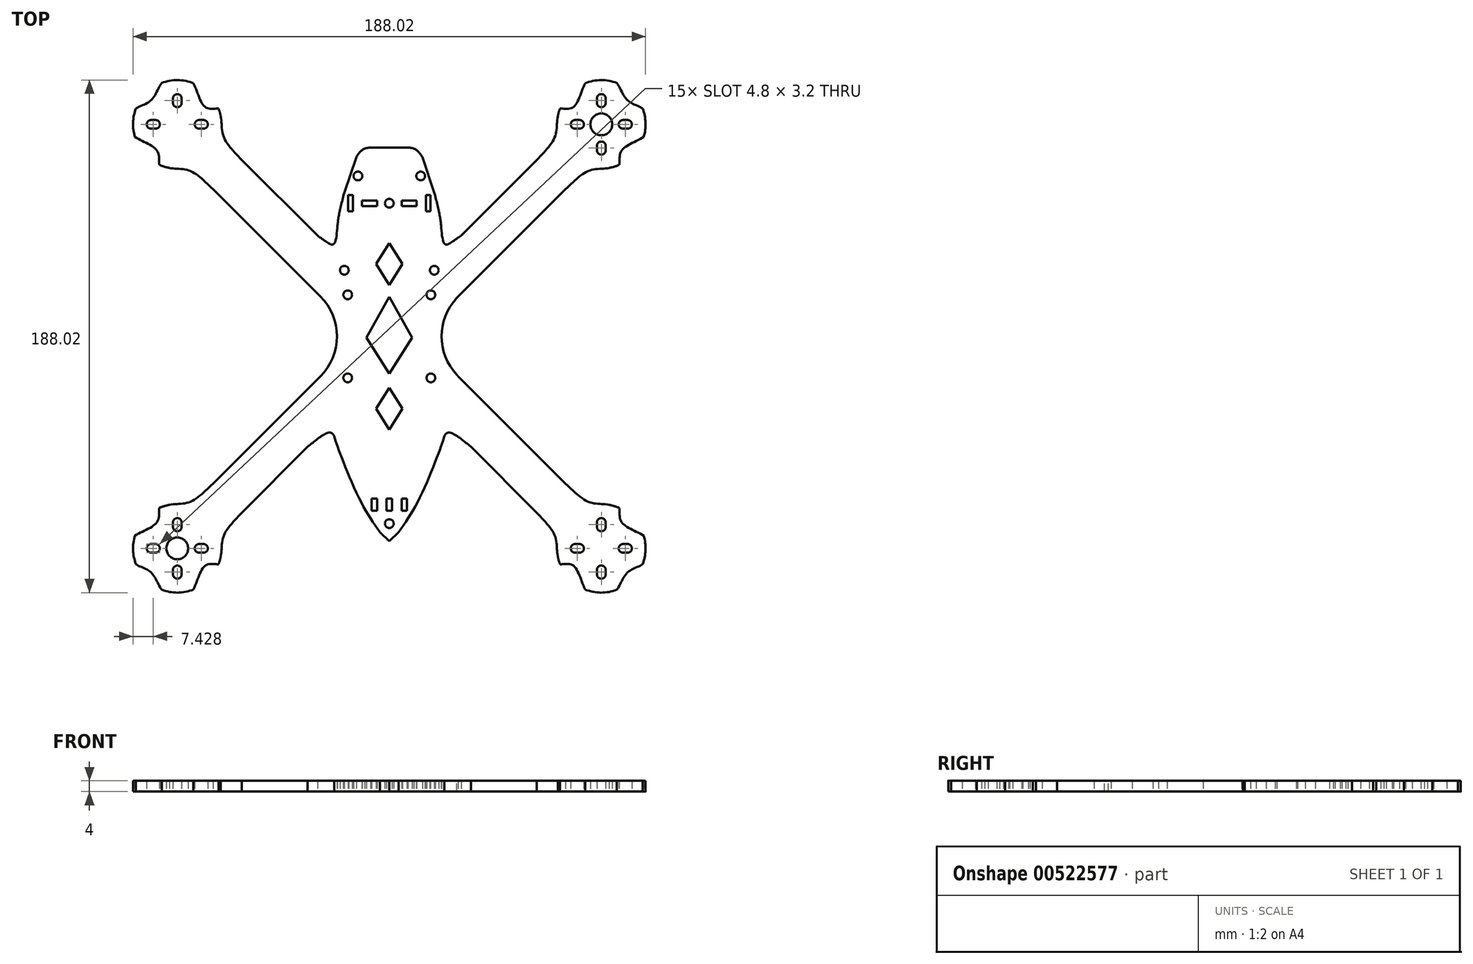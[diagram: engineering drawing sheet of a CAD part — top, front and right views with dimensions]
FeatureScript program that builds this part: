
annotation { "Feature Type Name" : "Feature", "Feature Type Description" : "" }
export const myFeature = defineFeature(function(context is Context, id is Id, definition is map)
    precondition{}
    {
        {
            var Q0;
            Q0=qCreatedBy(makeId("Top.planeOp"),FACE);
            var sketch = newSketch(context, id + "F0", { "sketchPlane" : qUnion([Q0])});
            skArc(sketch, "E0", {"start": v(79.38, 87.28) * mm, "mid": v(77.78, 88.88) * mm, "end": v(76.18, 87.28) * mm});
            skArc(sketch, "E1", {"start": v(69.78, 76.18) * mm, "mid": v(71.38, 77.78) * mm, "end": v(69.78, 79.38) * mm});
            skArc(sketch, "E2", {"start": v(76.18, 68.28) * mm, "mid": v(77.78, 66.68) * mm, "end": v(79.38, 68.28) * mm});
            skFitSpline(sketch, "E3", {"points": [v(54.07, 64.68) * mm, v(60.8, 73.32) * mm, v(61.81, 80.69) * mm], "startDerivative": vector(14.32, 15.77) * mm, "endDerivative": vector(3.24, 15.8) * mm});
            skFitSpline(sketch, "E4.MirrorCS", {"points": [v(64.68, 54.07) * mm, v(73.32, 60.8) * mm, v(80.69, 61.81) * mm], "startDerivative": vector(15.77, 14.32) * mm, "endDerivative": vector(15.8, 3.24) * mm});
            skArc(sketch, "E5.MirrorC", {"start": v(71.84, 92.89) * mm, "mid": v(77.65, 94.01) * mm, "end": v(83.48, 92.98) * mm});
            skArc(sketch, "E6.trimOffspring", {"start": v(61.81, 80.69) * mm, "mid": v(62.15, 82.16) * mm, "end": v(62.63, 83.6) * mm});
            skFitSpline(sketch, "E7", {"points": [v(62.63, 83.6) * mm, v(67.35, 84.01) * mm, v(71.84, 92.89) * mm], "startDerivative": vector(9.44, 0.18) * mm, "endDerivative": vector(7.72, 15.8) * mm});
            skFitSpline(sketch, "E8", {"points": [v(84.37, 62.95) * mm, v(85.15, 68.03) * mm, v(93.33, 73.14) * mm], "startDerivative": vector(1.43, 9.82) * mm, "endDerivative": vector(14.32, 9.05) * mm});
            skFitSpline(sketch, "E9", {"points": [v(92.94, 83.58) * mm, v(87.34, 86.65) * mm, v(83.48, 92.98) * mm], "startDerivative": vector(-9.53, 6.72) * mm, "endDerivative": vector(-7.98, 10.57) * mm});
            skArc(sketch, "E10.trimOffspring", {"start": v(92.94, 83.58) * mm, "mid": v(94, 78.4) * mm, "end": v(93.33, 73.14) * mm});
            skArc(sketch, "E11.trimOffspring", {"start": v(84.37, 62.95) * mm, "mid": v(82.56, 62.27) * mm, "end": v(80.69, 61.81) * mm});
            skCircle(sketch, "E12", {"center": v(77.78, 77.78) * mm, "radius": 4 * mm});
            skCircle(sketch, "E13.MirrorC", {"center": v(-77.78, 77.78) * mm, "radius": 4 * mm});
            skLineSegment(sketch, "E14.MirrorCS", {"start": v(-25.3, 14.68) * mm, "end": v(-64.68, 54.07) * mm});
            skCircle(sketch, "E15.MirrorC", {"center": v(77.78, -77.78) * mm, "radius": 4 * mm});
            skCircle(sketch, "E16.MirrorC", {"center": v(-77.78, -77.78) * mm, "radius": 4 * mm});
            skLineSegment(sketch, "E17.MirrorCS", {"start": v(-25.3, -14.68) * mm, "end": v(-64.68, -54.07) * mm});
            skLineSegment(sketch, "E18.MirrorCS", {"start": v(25.3, -14.68) * mm, "end": v(64.68, -54.07) * mm});
            skLineSegment(sketch, "E19.MirrorCS", {"start": v(27.36, -37.96) * mm, "end": v(54.07, -64.68) * mm});
            skLineSegment(sketch, "E20.MirrorCS", {"start": v(-27.36, -37.96) * mm, "end": v(-54.07, -64.68) * mm});
            skLineSegment(sketch, "E21.trimOffspring", {"start": v(-26.35, 36.96) * mm, "end": v(-54.07, 64.68) * mm});
            skLineSegment(sketch, "E22.trimOffspring", {"start": v(26.35, 36.96) * mm, "end": v(54.07, 64.68) * mm});
            skFitSpline(sketch, "E23", {"points": [v(29.93, -40.53) * mm, v(24.71, -36.48) * mm, v(21.1, -35.5) * mm, v(19, -47.4) * mm], "startDerivative": vector(-16.04, 13.48) * mm, "endDerivative": vector(-1.52, -37.22) * mm});
            skFitSpline(sketch, "E24.MirrorCS", {"points": [v(-29.93, -40.53) * mm, v(-24.71, -36.48) * mm, v(-21.1, -35.5) * mm, v(-19, -47.4) * mm], "startDerivative": vector(16.04, 13.48) * mm, "endDerivative": vector(1.52, -37.22) * mm});
            skFitSpline(sketch, "E25", {"points": [v(-12.14, 65.75) * mm, v(-10.16, 68.18) * mm, v(-6.56, 70) * mm], "startDerivative": vector(3.6, 5.61) * mm, "endDerivative": vector(7.46, 2.94) * mm});
            skFitSpline(sketch, "E26", {"points": [v(-19, 40.7) * mm, v(-18.4, 44.88) * mm, v(-16.56, 52.62) * mm], "startDerivative": vector(1.06, 9.2) * mm, "endDerivative": vector(3.7, 14.37) * mm});
            skLineSegment(sketch, "E27", {"start": v(-16.56, 52.62) * mm, "end": v(-12.14, 65.75) * mm});
            skFitSpline(sketch, "E28.MirrorCS", {"points": [v(12.14, 65.75) * mm, v(10.16, 68.18) * mm, v(6.56, 70) * mm], "startDerivative": vector(-3.6, 5.61) * mm, "endDerivative": vector(-7.46, 2.94) * mm});
            skFitSpline(sketch, "E29.MirrorCS", {"points": [v(19, 40.7) * mm, v(18.4, 44.88) * mm, v(16.56, 52.62) * mm], "startDerivative": vector(-1.06, 9.2) * mm, "endDerivative": vector(-3.7, 14.37) * mm});
            skLineSegment(sketch, "E30.MirrorCS", {"start": v(16.56, 52.62) * mm, "end": v(12.14, 65.75) * mm});
            skFitSpline(sketch, "E31", {"points": [v(-9.06, 68.9) * mm, v(-6.8, 69.3) * mm, v(-4.56, 69.08) * mm], "startDerivative": vector(4.47, 1.15) * mm, "endDerivative": vector(4.51, -0.76) * mm});
            skFitSpline(sketch, "E32.MirrorCS", {"points": [v(9.06, 68.9) * mm, v(6.8, 69.3) * mm, v(4.56, 69.08) * mm], "startDerivative": vector(-4.47, 1.15) * mm, "endDerivative": vector(-4.51, -0.76) * mm});
            skFitSpline(sketch, "E33.MirrorCS", {"points": [v(25.3, 14.68) * mm, v(21.09, 9.2) * mm, v(19, 0) * mm], "startDerivative": vector(-10.32, -10.71) * mm, "endDerivative": vector(-2.46, -18.46) * mm});
            skFitSpline(sketch, "E34.MirrorCS", {"points": [v(25.3, -14.68) * mm, v(21.09, -9.2) * mm, v(19, 0) * mm], "startDerivative": vector(-10.32, 10.71) * mm, "endDerivative": vector(-2.46, 18.46) * mm});
            skFitSpline(sketch, "E35", {"points": [v(-26.35, 36.96) * mm, v(-23.17, 34.76) * mm, v(-20.57, 33.73) * mm, v(-19, 40.7) * mm], "startDerivative": vector(10, -6.85) * mm, "endDerivative": vector(1.76, 22.78) * mm});
            skFitSpline(sketch, "E36.MirrorCS", {"points": [v(26.35, 36.96) * mm, v(23.17, 34.76) * mm, v(20.57, 33.73) * mm, v(19, 40.7) * mm], "startDerivative": vector(-10, -6.85) * mm, "endDerivative": vector(-1.76, 22.78) * mm});
            skLineSegment(sketch, "E37", {"start": v(-6.8, 69.3) * mm, "end": v(6.8, 69.3) * mm});
            skLineSegment(sketch, "E38", {"start": v(-3.49, -71.8) * mm, "end": v(0, -75.2) * mm});
            skLineSegment(sketch, "E39", {"start": v(0, -75.2) * mm, "end": v(3.49, -71.8) * mm});
            skPoint(sketch, "E40", {"position": v(0, -68.7) * mm});
            skCircle(sketch, "E41", {"center": v(0, -68.7) * mm, "radius": 1.6 * mm});
            skPoint(sketch, "E42", {"position": v(-16.5, 24.27) * mm});
            skCircle(sketch, "E43", {"center": v(-16.5, 24.27) * mm, "radius": 1.6 * mm});
            skCircle(sketch, "E44.MirrorC", {"center": v(16.5, 24.27) * mm, "radius": 1.6 * mm});
            skLineSegment(sketch, "E45.trimOffspring", {"start": v(25.3, 14.68) * mm, "end": v(64.68, 54.07) * mm});
            skCircle(sketch, "E46", {"center": v(-11.5, 58.84) * mm, "radius": 1.6 * mm});
            skLineSegment(sketch, "E47.bottom", {"start": v(-14.25, 45.84) * mm, "end": v(-15.1, 45.84) * mm});
            skLineSegment(sketch, "E47.top", {"start": v(-14.25, 51.84) * mm, "end": v(-15.1, 51.84) * mm});
            skPoint(sketch, "E48", {"position": v(-14.25, 48.84) * mm});
            skPoint(sketch, "E49.endSnap0", {"position": v(0, 69.3) * mm});
            skFitSpline(sketch, "E50", {"points": [v(-20.24, -36.7) * mm, v(-18.2, -42.52) * mm, v(-10.72, -60.08) * mm, v(-3.49, -71.8) * mm], "startDerivative": vector(6.97, -20.75) * mm, "endDerivative": vector(20.48, -29.65) * mm});
            skFitSpline(sketch, "E51.MirrorCS", {"points": [v(20.24, -36.7) * mm, v(18.2, -42.52) * mm, v(10.72, -60.08) * mm, v(3.49, -71.8) * mm], "startDerivative": vector(-6.97, -20.75) * mm, "endDerivative": vector(-20.48, -29.65) * mm});
            skPoint(sketch, "E52.orphan", {"position": v(-6.97, -68.4) * mm});
            skPoint(sketch, "E53.orphan", {"position": v(6.97, -68.4) * mm});
            skPoint(sketch, "E54", {"position": v(0.05, 59.65) * mm});
            skPoint(sketch, "E55", {"position": v(0.05, 15.16) * mm});
            skPoint(sketch, "E56", {"position": v(-15.25, 0) * mm});
            skPoint(sketch, "E57", {"position": v(0, 15.25) * mm});
            skCircle(sketch, "E58", {"center": v(-15.25, 15.25) * mm, "radius": 1.6 * mm});
            skCircle(sketch, "E59.MirrorC", {"center": v(15.25, 15.25) * mm, "radius": 1.6 * mm});
            skCircle(sketch, "E60.MirrorC", {"center": v(-15.25, -15.25) * mm, "radius": 1.6 * mm});
            skCircle(sketch, "E61.MirrorC", {"center": v(15.25, -15.25) * mm, "radius": 1.6 * mm});
            skPoint(sketch, "E62", {"position": v(5.5, -61.74) * mm});
            skLineSegment(sketch, "E63.bottom", {"start": v(4.5, -59.49) * mm, "end": v(6.5, -59.49) * mm});
            skLineSegment(sketch, "E63.top", {"start": v(4.5, -63.99) * mm, "end": v(6.5, -63.99) * mm});
            skLineSegment(sketch, "E63.left", {"start": v(4.5, -59.49) * mm, "end": v(4.5, -63.99) * mm});
            skLineSegment(sketch, "E63.right", {"start": v(6.5, -59.49) * mm, "end": v(6.5, -63.99) * mm});
            skPoint(sketch, "E64.MirrorP", {"position": v(-5.5, -61.74) * mm});
            skLineSegment(sketch, "E65.MirrorCS", {"start": v(-6.5, -59.49) * mm, "end": v(-6.5, -63.99) * mm});
            skLineSegment(sketch, "E66.MirrorCS", {"start": v(-4.5, -59.49) * mm, "end": v(-4.5, -63.99) * mm});
            skLineSegment(sketch, "E67.MirrorCS", {"start": v(-4.5, -63.99) * mm, "end": v(-6.5, -63.99) * mm});
            skLineSegment(sketch, "E68.MirrorCS", {"start": v(-4.5, -59.49) * mm, "end": v(-6.5, -59.49) * mm});
            skPoint(sketch, "E69", {"position": v(0, -61.74) * mm});
            skPoint(sketch, "E69.positionSnap0", {"position": v(-4.5, -61.74) * mm});
            skLineSegment(sketch, "E70.bottom", {"start": v(1, -59.49) * mm, "end": v(-1, -59.49) * mm});
            skLineSegment(sketch, "E70.top", {"start": v(1, -63.99) * mm, "end": v(-1, -63.99) * mm});
            skLineSegment(sketch, "E70.left", {"start": v(1, -59.49) * mm, "end": v(1, -63.99) * mm});
            skLineSegment(sketch, "E70.right", {"start": v(-1, -59.49) * mm, "end": v(-1, -63.99) * mm});
            skLineSegment(sketch, "E71", {"start": v(-15.1, 51.84) * mm, "end": v(-15.1, 45.84) * mm});
            skLineSegment(sketch, "E72.MirrorCS", {"start": v(-14.25, 51.84) * mm, "end": v(-13.4, 51.84) * mm});
            skLineSegment(sketch, "E73.MirrorCS", {"start": v(-14.25, 45.84) * mm, "end": v(-13.4, 45.84) * mm});
            skPoint(sketch, "E74.MirrorP", {"position": v(-14.25, 42.77) * mm});
            skLineSegment(sketch, "E75.MirrorCS", {"start": v(-13.4, 51.84) * mm, "end": v(-13.4, 45.84) * mm});
            skPoint(sketch, "E76.orphan", {"position": v(-12.55, 45.84) * mm});
            skPoint(sketch, "E77.orphan", {"position": v(-12.55, 51.84) * mm});
            skPoint(sketch, "E78.orphan", {"position": v(-15.95, 51.84) * mm});
            skPoint(sketch, "E79.orphan", {"position": v(-15.95, 45.84) * mm});
            skLineSegment(sketch, "E80.MirrorCS", {"start": v(14.25, 45.84) * mm, "end": v(15.1, 45.84) * mm});
            skLineSegment(sketch, "E81.MirrorCS", {"start": v(14.25, 45.84) * mm, "end": v(13.4, 45.84) * mm});
            skLineSegment(sketch, "E82.MirrorCS", {"start": v(14.25, 51.84) * mm, "end": v(13.4, 51.84) * mm});
            skLineSegment(sketch, "E83.MirrorCS", {"start": v(14.25, 51.84) * mm, "end": v(15.1, 51.84) * mm});
            skPoint(sketch, "E84.MirrorP", {"position": v(14.25, 42.77) * mm});
            skLineSegment(sketch, "E85.MirrorCS", {"start": v(15.1, 51.84) * mm, "end": v(15.1, 45.84) * mm});
            skPoint(sketch, "E86.MirrorP", {"position": v(15.95, 45.84) * mm});
            skPoint(sketch, "E87.MirrorP", {"position": v(15.95, 51.84) * mm});
            skPoint(sketch, "E88.MirrorP", {"position": v(12.55, 51.84) * mm});
            skPoint(sketch, "E89.MirrorP", {"position": v(12.55, 45.84) * mm});
            skPoint(sketch, "E90.MirrorP", {"position": v(14.25, 48.84) * mm});
            skLineSegment(sketch, "E91.MirrorCS", {"start": v(13.4, 51.84) * mm, "end": v(13.4, 45.84) * mm});
            skCircle(sketch, "E92.MirrorC", {"center": v(11.5, 58.84) * mm, "radius": 1.6 * mm});
            skPoint(sketch, "E93", {"position": v(88.51, 77.78) * mm});
            skPoint(sketch, "E94", {"position": v(68.18, 77.78) * mm});
            skPoint(sketch, "E95", {"position": v(87.38, 77.78) * mm});
            skPoint(sketch, "E96", {"position": v(77.78, 85.68) * mm});
            skPoint(sketch, "E97", {"position": v(77.78, 69.88) * mm});
            skArc(sketch, "E98", {"start": v(76.18, 85.68) * mm, "mid": v(77.78, 84.08) * mm, "end": v(79.38, 85.68) * mm});
            skArc(sketch, "E99", {"start": v(68.18, 79.38) * mm, "mid": v(66.58, 77.78) * mm, "end": v(68.18, 76.18) * mm});
            skArc(sketch, "E100", {"start": v(79.38, 69.88) * mm, "mid": v(77.78, 71.48) * mm, "end": v(76.18, 69.88) * mm});
            skPoint(sketch, "E101", {"position": v(69.78, 76.18) * mm});
            skPoint(sketch, "E102", {"position": v(69.78, 79.38) * mm});
            skPoint(sketch, "E103", {"position": v(68.18, 76.18) * mm});
            skPoint(sketch, "E104", {"position": v(68.18, 79.38) * mm});
            skLineSegment(sketch, "E105", {"start": v(68.18, 79.38) * mm, "end": v(69.78, 79.38) * mm});
            skLineSegment(sketch, "E106", {"start": v(69.78, 76.18) * mm, "end": v(68.18, 76.18) * mm});
            skPoint(sketch, "E107.start.orphan", {"position": v(66.08, 77.78) * mm});
            skPoint(sketch, "E108", {"position": v(76.18, 69.88) * mm});
            skPoint(sketch, "E109", {"position": v(79.38, 69.88) * mm});
            skPoint(sketch, "E110", {"position": v(79.38, 68.28) * mm});
            skPoint(sketch, "E111", {"position": v(76.18, 68.28) * mm});
            skLineSegment(sketch, "E112", {"start": v(76.18, 69.88) * mm, "end": v(76.18, 68.28) * mm});
            skLineSegment(sketch, "E113", {"start": v(79.38, 68.28) * mm, "end": v(79.38, 69.88) * mm});
            skPoint(sketch, "E114", {"position": v(85.78, 79.38) * mm});
            skPoint(sketch, "E115", {"position": v(85.78, 76.18) * mm});
            skPoint(sketch, "E116", {"position": v(84.18, 79.38) * mm});
            skPoint(sketch, "E117", {"position": v(84.18, 76.18) * mm});
            skPoint(sketch, "E118", {"position": v(79.38, 87.28) * mm});
            skPoint(sketch, "E119", {"position": v(79.38, 85.68) * mm});
            skPoint(sketch, "E120", {"position": v(76.18, 85.68) * mm});
            skPoint(sketch, "E121", {"position": v(76.18, 87.28) * mm});
            skLineSegment(sketch, "E122", {"start": v(76.18, 87.28) * mm, "end": v(76.18, 85.68) * mm});
            skLineSegment(sketch, "E123", {"start": v(79.38, 87.28) * mm, "end": v(79.38, 85.68) * mm});
            skArc(sketch, "E124", {"start": v(85.78, 79.38) * mm, "mid": v(84.18, 77.78) * mm, "end": v(85.78, 76.18) * mm});
            skArc(sketch, "E125", {"start": v(87.38, 76.18) * mm, "mid": v(88.98, 77.78) * mm, "end": v(87.38, 79.38) * mm});
            skPoint(sketch, "E126", {"position": v(87.38, 79.38) * mm});
            skPoint(sketch, "E127", {"position": v(87.38, 76.18) * mm});
            skLineSegment(sketch, "E128", {"start": v(85.78, 79.38) * mm, "end": v(87.38, 79.38) * mm});
            skLineSegment(sketch, "E129", {"start": v(85.78, 76.18) * mm, "end": v(87.38, 76.18) * mm});
            skLineSegment(sketch, "E130", {"start": v(0, 0) * mm, "end": v(0, 0) * mm});
            skArc(sketch, "E131.MirrorCS", {"start": v(-79.38, 87.28) * mm, "mid": v(-77.78, 88.88) * mm, "end": v(-76.18, 87.28) * mm});
            skArc(sketch, "E132.MirrorCS", {"start": v(-69.78, 76.18) * mm, "mid": v(-71.38, 77.78) * mm, "end": v(-69.78, 79.38) * mm});
            skArc(sketch, "E133.MirrorCS", {"start": v(-76.18, 68.28) * mm, "mid": v(-77.78, 66.68) * mm, "end": v(-79.38, 68.28) * mm});
            skLineSegment(sketch, "E134.MirrorCS", {"start": v(-79.38, 68.28) * mm, "end": v(-79.38, 69.88) * mm});
            skArc(sketch, "E135.MirrorCS", {"start": v(-68.18, 79.38) * mm, "mid": v(-66.58, 77.78) * mm, "end": v(-68.18, 76.18) * mm});
            skLineSegment(sketch, "E136.MirrorCS", {"start": v(-76.18, 87.28) * mm, "end": v(-76.18, 85.68) * mm});
            skArc(sketch, "E137.MirrorCS", {"start": v(-84.37, 62.95) * mm, "mid": v(-82.56, 62.27) * mm, "end": v(-80.69, 61.81) * mm});
            skLineSegment(sketch, "E138.MirrorCS", {"start": v(-79.38, 87.28) * mm, "end": v(-79.38, 85.68) * mm});
            skArc(sketch, "E139.MirrorCS", {"start": v(-85.78, 79.38) * mm, "mid": v(-84.18, 77.78) * mm, "end": v(-85.78, 76.18) * mm});
            skArc(sketch, "E140.MirrorCS", {"start": v(-79.38, 69.88) * mm, "mid": v(-77.78, 71.48) * mm, "end": v(-76.18, 69.88) * mm});
            skLineSegment(sketch, "E141.MirrorCS", {"start": v(-85.78, 79.38) * mm, "end": v(-87.38, 79.38) * mm});
            skArc(sketch, "E142.MirrorCS", {"start": v(-87.38, 76.18) * mm, "mid": v(-88.98, 77.78) * mm, "end": v(-87.38, 79.38) * mm});
            skLineSegment(sketch, "E143.MirrorCS", {"start": v(-85.78, 76.18) * mm, "end": v(-87.38, 76.18) * mm});
            skArc(sketch, "E144.MirrorCS", {"start": v(-76.18, 85.68) * mm, "mid": v(-77.78, 84.08) * mm, "end": v(-79.38, 85.68) * mm});
            skLineSegment(sketch, "E145.MirrorCS", {"start": v(-69.78, 76.18) * mm, "end": v(-68.18, 76.18) * mm});
            skLineSegment(sketch, "E146.MirrorCS", {"start": v(-76.18, 69.88) * mm, "end": v(-76.18, 68.28) * mm});
            skArc(sketch, "E147.MirrorCS", {"start": v(-61.81, 80.69) * mm, "mid": v(-62.15, 82.16) * mm, "end": v(-62.63, 83.6) * mm});
            skLineSegment(sketch, "E148.MirrorCS", {"start": v(-68.18, 79.38) * mm, "end": v(-69.78, 79.38) * mm});
            skFitSpline(sketch, "E149.MirrorCS", {"points": [v(-64.68, 54.07) * mm, v(-73.32, 60.8) * mm, v(-80.69, 61.81) * mm], "startDerivative": vector(-15.77, 14.32) * mm, "endDerivative": vector(-15.8, 3.24) * mm});
            skFitSpline(sketch, "E150.MirrorCS", {"points": [v(-62.63, 83.6) * mm, v(-67.35, 84.01) * mm, v(-71.84, 92.89) * mm], "startDerivative": vector(-9.44, 0.18) * mm, "endDerivative": vector(-7.72, 15.8) * mm});
            skFitSpline(sketch, "E151.MirrorCS", {"points": [v(-84.37, 62.95) * mm, v(-85.15, 68.03) * mm, v(-93.33, 73.14) * mm], "startDerivative": vector(-1.43, 9.82) * mm, "endDerivative": vector(-14.32, 9.05) * mm});
            skFitSpline(sketch, "E152.MirrorCS", {"points": [v(-92.94, 83.58) * mm, v(-87.34, 86.65) * mm, v(-83.48, 92.98) * mm], "startDerivative": vector(9.53, 6.72) * mm, "endDerivative": vector(7.98, 10.57) * mm});
            skArc(sketch, "E153.MirrorCS", {"start": v(-92.94, 83.58) * mm, "mid": v(-94, 78.4) * mm, "end": v(-93.33, 73.14) * mm});
            skFitSpline(sketch, "E154.MirrorCS", {"points": [v(-54.07, 64.68) * mm, v(-60.8, 73.32) * mm, v(-61.81, 80.69) * mm], "startDerivative": vector(-14.32, 15.77) * mm, "endDerivative": vector(-3.24, 15.8) * mm});
            skPoint(sketch, "E155.MirrorP", {"position": v(-79.38, 69.88) * mm});
            skPoint(sketch, "E156.MirrorP", {"position": v(-79.38, 85.68) * mm});
            skPoint(sketch, "E157.MirrorP", {"position": v(-76.18, 85.68) * mm});
            skArc(sketch, "E158.MirrorCS", {"start": v(-71.84, 92.89) * mm, "mid": v(-77.65, 94.01) * mm, "end": v(-83.48, 92.98) * mm});
            skPoint(sketch, "E159.MirrorP", {"position": v(-84.18, 79.38) * mm});
            skPoint(sketch, "E160.MirrorP", {"position": v(-85.78, 76.18) * mm});
            skPoint(sketch, "E161.MirrorP", {"position": v(-79.38, 87.28) * mm});
            skPoint(sketch, "E162.MirrorP", {"position": v(-84.18, 76.18) * mm});
            skPoint(sketch, "E163.MirrorP", {"position": v(-76.18, 87.28) * mm});
            skPoint(sketch, "E164.MirrorP", {"position": v(-69.78, 79.38) * mm});
            skPoint(sketch, "E165.MirrorP", {"position": v(-68.18, 76.18) * mm});
            skPoint(sketch, "E166.MirrorP", {"position": v(-87.38, 76.18) * mm});
            skPoint(sketch, "E167.MirrorP", {"position": v(-66.08, 77.78) * mm});
            skPoint(sketch, "E168.MirrorP", {"position": v(-68.18, 79.38) * mm});
            skPoint(sketch, "E169.MirrorP", {"position": v(-87.38, 79.38) * mm});
            skPoint(sketch, "E170.MirrorP", {"position": v(-76.18, 68.28) * mm});
            skPoint(sketch, "E171.MirrorP", {"position": v(-88.51, 77.78) * mm});
            skPoint(sketch, "E172.MirrorP", {"position": v(-85.78, 79.38) * mm});
            skPoint(sketch, "E173.MirrorP", {"position": v(-76.18, 69.88) * mm});
            skPoint(sketch, "E174.MirrorP", {"position": v(-79.38, 68.28) * mm});
            skPoint(sketch, "E175.MirrorP", {"position": v(-69.78, 76.18) * mm});
            skLineSegment(sketch, "E176.MirrorCS", {"start": v(76.18, -87.28) * mm, "end": v(76.18, -85.68) * mm});
            skLineSegment(sketch, "E177.MirrorCS", {"start": v(79.38, -68.28) * mm, "end": v(79.38, -69.88) * mm});
            skLineSegment(sketch, "E178.MirrorCS", {"start": v(79.38, -87.28) * mm, "end": v(79.38, -85.68) * mm});
            skLineSegment(sketch, "E179.MirrorCS", {"start": v(76.18, -69.88) * mm, "end": v(76.18, -68.28) * mm});
            skArc(sketch, "E180.MirrorCS", {"start": v(76.18, -68.28) * mm, "mid": v(77.78, -66.68) * mm, "end": v(79.38, -68.28) * mm});
            skArc(sketch, "E181.MirrorCS", {"start": v(79.38, -87.28) * mm, "mid": v(77.78, -88.88) * mm, "end": v(76.18, -87.28) * mm});
            skArc(sketch, "E182.MirrorCS", {"start": v(79.38, -69.88) * mm, "mid": v(77.78, -71.48) * mm, "end": v(76.18, -69.88) * mm});
            skArc(sketch, "E183.MirrorCS", {"start": v(76.18, -85.68) * mm, "mid": v(77.78, -84.08) * mm, "end": v(79.38, -85.68) * mm});
            skLineSegment(sketch, "E184.MirrorCS", {"start": v(85.78, -79.38) * mm, "end": v(87.38, -79.38) * mm});
            skArc(sketch, "E185.MirrorCS", {"start": v(68.18, -79.38) * mm, "mid": v(66.58, -77.78) * mm, "end": v(68.18, -76.18) * mm});
            skArc(sketch, "E186.MirrorCS", {"start": v(69.78, -76.18) * mm, "mid": v(71.38, -77.78) * mm, "end": v(69.78, -79.38) * mm});
            skLineSegment(sketch, "E187.MirrorCS", {"start": v(69.78, -76.18) * mm, "end": v(68.18, -76.18) * mm});
            skArc(sketch, "E188.MirrorCS", {"start": v(61.81, -80.69) * mm, "mid": v(62.15, -82.16) * mm, "end": v(62.63, -83.6) * mm});
            skLineSegment(sketch, "E189.MirrorCS", {"start": v(68.18, -79.38) * mm, "end": v(69.78, -79.38) * mm});
            skArc(sketch, "E190.MirrorCS", {"start": v(87.38, -76.18) * mm, "mid": v(88.98, -77.78) * mm, "end": v(87.38, -79.38) * mm});
            skArc(sketch, "E191.MirrorCS", {"start": v(85.78, -79.38) * mm, "mid": v(84.18, -77.78) * mm, "end": v(85.78, -76.18) * mm});
            skLineSegment(sketch, "E192.MirrorCS", {"start": v(85.78, -76.18) * mm, "end": v(87.38, -76.18) * mm});
            skArc(sketch, "E193.MirrorCS", {"start": v(84.37, -62.95) * mm, "mid": v(82.56, -62.27) * mm, "end": v(80.69, -61.81) * mm});
            skFitSpline(sketch, "E194.MirrorCS", {"points": [v(84.37, -62.95) * mm, v(85.15, -68.03) * mm, v(93.33, -73.14) * mm], "startDerivative": vector(1.43, -9.82) * mm, "endDerivative": vector(14.32, -9.05) * mm});
            skFitSpline(sketch, "E195.MirrorCS", {"points": [v(92.94, -83.58) * mm, v(87.34, -86.65) * mm, v(83.48, -92.98) * mm], "startDerivative": vector(-9.53, -6.72) * mm, "endDerivative": vector(-7.98, -10.57) * mm});
            skFitSpline(sketch, "E196.MirrorCS", {"points": [v(62.63, -83.6) * mm, v(67.35, -84.01) * mm, v(71.84, -92.89) * mm], "startDerivative": vector(9.44, -0.18) * mm, "endDerivative": vector(7.72, -15.8) * mm});
            skArc(sketch, "E197.MirrorCS", {"start": v(92.94, -83.58) * mm, "mid": v(94, -78.4) * mm, "end": v(93.33, -73.14) * mm});
            skArc(sketch, "E198.MirrorCS", {"start": v(71.84, -92.89) * mm, "mid": v(77.65, -94.01) * mm, "end": v(83.48, -92.98) * mm});
            skFitSpline(sketch, "E199.MirrorCS", {"points": [v(54.07, -64.68) * mm, v(60.8, -73.32) * mm, v(61.81, -80.69) * mm], "startDerivative": vector(14.32, -15.77) * mm, "endDerivative": vector(3.24, -15.8) * mm});
            skFitSpline(sketch, "E200.MirrorCS", {"points": [v(64.68, -54.07) * mm, v(73.32, -60.8) * mm, v(80.69, -61.81) * mm], "startDerivative": vector(15.77, -14.32) * mm, "endDerivative": vector(15.8, -3.24) * mm});
            skPoint(sketch, "E201.MirrorP", {"position": v(79.38, -69.88) * mm});
            skPoint(sketch, "E202.MirrorP", {"position": v(79.38, -68.28) * mm});
            skPoint(sketch, "E203.MirrorP", {"position": v(69.78, -79.38) * mm});
            skPoint(sketch, "E204.MirrorP", {"position": v(69.78, -76.18) * mm});
            skPoint(sketch, "E205.MirrorP", {"position": v(84.18, -76.18) * mm});
            skPoint(sketch, "E206.MirrorP", {"position": v(76.18, -85.68) * mm});
            skPoint(sketch, "E207.MirrorP", {"position": v(79.38, -87.28) * mm});
            skPoint(sketch, "E208.MirrorP", {"position": v(85.78, -76.18) * mm});
            skPoint(sketch, "E209.MirrorP", {"position": v(84.18, -79.38) * mm});
            skPoint(sketch, "E210.MirrorP", {"position": v(76.18, -69.88) * mm});
            skPoint(sketch, "E211.MirrorP", {"position": v(88.51, -77.78) * mm});
            skPoint(sketch, "E212.MirrorP", {"position": v(76.18, -87.28) * mm});
            skPoint(sketch, "E213.MirrorP", {"position": v(85.78, -79.38) * mm});
            skPoint(sketch, "E214.MirrorP", {"position": v(76.18, -68.28) * mm});
            skPoint(sketch, "E215.MirrorP", {"position": v(68.18, -76.18) * mm});
            skPoint(sketch, "E216.MirrorP", {"position": v(87.38, -76.18) * mm});
            skPoint(sketch, "E217.MirrorP", {"position": v(87.38, -79.38) * mm});
            skPoint(sketch, "E218.MirrorP", {"position": v(68.18, -79.38) * mm});
            skPoint(sketch, "E219.MirrorP", {"position": v(79.38, -85.68) * mm});
            skPoint(sketch, "E220.MirrorP", {"position": v(66.08, -77.78) * mm});
            skArc(sketch, "E221.MirrorCS", {"start": v(-79.38, -69.88) * mm, "mid": v(-77.78, -71.48) * mm, "end": v(-76.18, -69.88) * mm});
            skArc(sketch, "E222.MirrorCS", {"start": v(-85.78, -79.38) * mm, "mid": v(-84.18, -77.78) * mm, "end": v(-85.78, -76.18) * mm});
            skArc(sketch, "E223.MirrorCS", {"start": v(-87.38, -76.18) * mm, "mid": v(-88.98, -77.78) * mm, "end": v(-87.38, -79.38) * mm});
            skLineSegment(sketch, "E224.MirrorCS", {"start": v(-85.78, -79.38) * mm, "end": v(-87.38, -79.38) * mm});
            skLineSegment(sketch, "E225.MirrorCS", {"start": v(-79.38, -68.28) * mm, "end": v(-79.38, -69.88) * mm});
            skArc(sketch, "E226.MirrorCS", {"start": v(-76.18, -68.28) * mm, "mid": v(-77.78, -66.68) * mm, "end": v(-79.38, -68.28) * mm});
            skArc(sketch, "E227.MirrorCS", {"start": v(-92.94, -83.58) * mm, "mid": v(-94, -78.4) * mm, "end": v(-93.33, -73.14) * mm});
            skArc(sketch, "E228.MirrorCS", {"start": v(-84.37, -62.95) * mm, "mid": v(-82.56, -62.27) * mm, "end": v(-80.69, -61.81) * mm});
            skArc(sketch, "E229.MirrorCS", {"start": v(-61.81, -80.69) * mm, "mid": v(-62.15, -82.16) * mm, "end": v(-62.63, -83.6) * mm});
            skFitSpline(sketch, "E230.MirrorCS", {"points": [v(-92.94, -83.58) * mm, v(-87.34, -86.65) * mm, v(-83.48, -92.98) * mm], "startDerivative": vector(9.53, -6.72) * mm, "endDerivative": vector(7.98, -10.57) * mm});
            skFitSpline(sketch, "E231.MirrorCS", {"points": [v(-84.37, -62.95) * mm, v(-85.15, -68.03) * mm, v(-93.33, -73.14) * mm], "startDerivative": vector(-1.43, -9.82) * mm, "endDerivative": vector(-14.32, -9.05) * mm});
            skLineSegment(sketch, "E232.MirrorCS", {"start": v(-85.78, -76.18) * mm, "end": v(-87.38, -76.18) * mm});
            skLineSegment(sketch, "E233.MirrorCS", {"start": v(-76.18, -69.88) * mm, "end": v(-76.18, -68.28) * mm});
            skArc(sketch, "E234.MirrorCS", {"start": v(-71.84, -92.89) * mm, "mid": v(-77.65, -94.01) * mm, "end": v(-83.48, -92.98) * mm});
            skLineSegment(sketch, "E235.MirrorCS", {"start": v(-79.38, -87.28) * mm, "end": v(-79.38, -85.68) * mm});
            skArc(sketch, "E236.MirrorCS", {"start": v(-68.18, -79.38) * mm, "mid": v(-66.58, -77.78) * mm, "end": v(-68.18, -76.18) * mm});
            skArc(sketch, "E237.MirrorCS", {"start": v(-76.18, -85.68) * mm, "mid": v(-77.78, -84.08) * mm, "end": v(-79.38, -85.68) * mm});
            skLineSegment(sketch, "E238.MirrorCS", {"start": v(-76.18, -87.28) * mm, "end": v(-76.18, -85.68) * mm});
            skArc(sketch, "E239.MirrorCS", {"start": v(-79.38, -87.28) * mm, "mid": v(-77.78, -88.88) * mm, "end": v(-76.18, -87.28) * mm});
            skLineSegment(sketch, "E240.MirrorCS", {"start": v(-68.18, -79.38) * mm, "end": v(-69.78, -79.38) * mm});
            skFitSpline(sketch, "E241.MirrorCS", {"points": [v(-62.63, -83.6) * mm, v(-67.35, -84.01) * mm, v(-71.84, -92.89) * mm], "startDerivative": vector(-9.44, -0.18) * mm, "endDerivative": vector(-7.72, -15.8) * mm});
            skLineSegment(sketch, "E242.MirrorCS", {"start": v(-69.78, -76.18) * mm, "end": v(-68.18, -76.18) * mm});
            skArc(sketch, "E243.MirrorCS", {"start": v(-69.78, -76.18) * mm, "mid": v(-71.38, -77.78) * mm, "end": v(-69.78, -79.38) * mm});
            skFitSpline(sketch, "E244.MirrorCS", {"points": [v(-54.07, -64.68) * mm, v(-60.8, -73.32) * mm, v(-61.81, -80.69) * mm], "startDerivative": vector(-14.32, -15.77) * mm, "endDerivative": vector(-3.24, -15.8) * mm});
            skFitSpline(sketch, "E245.MirrorCS", {"points": [v(-64.68, -54.07) * mm, v(-73.32, -60.8) * mm, v(-80.69, -61.81) * mm], "startDerivative": vector(-15.77, -14.32) * mm, "endDerivative": vector(-15.8, -3.24) * mm});
            skPoint(sketch, "E246.MirrorP", {"position": v(-85.78, -76.18) * mm});
            skPoint(sketch, "E247.MirrorP", {"position": v(-79.38, -68.28) * mm});
            skPoint(sketch, "E248.MirrorP", {"position": v(-76.18, -85.68) * mm});
            skPoint(sketch, "E249.MirrorP", {"position": v(-79.38, -85.68) * mm});
            skPoint(sketch, "E250.MirrorP", {"position": v(-76.18, -68.28) * mm});
            skPoint(sketch, "E251.MirrorP", {"position": v(-84.18, -79.38) * mm});
            skPoint(sketch, "E252.MirrorP", {"position": v(-84.18, -76.18) * mm});
            skPoint(sketch, "E253.MirrorP", {"position": v(-69.78, -76.18) * mm});
            skPoint(sketch, "E254.MirrorP", {"position": v(-69.78, -79.38) * mm});
            skPoint(sketch, "E255.MirrorP", {"position": v(-76.18, -69.88) * mm});
            skPoint(sketch, "E256.MirrorP", {"position": v(-79.38, -69.88) * mm});
            skPoint(sketch, "E257.MirrorP", {"position": v(-87.38, -76.18) * mm});
            skPoint(sketch, "E258.MirrorP", {"position": v(-66.08, -77.78) * mm});
            skPoint(sketch, "E259.MirrorP", {"position": v(-68.18, -76.18) * mm});
            skPoint(sketch, "E260.MirrorP", {"position": v(-76.18, -87.28) * mm});
            skPoint(sketch, "E261.MirrorP", {"position": v(-88.51, -77.78) * mm});
            skPoint(sketch, "E262.MirrorP", {"position": v(-87.38, -79.38) * mm});
            skPoint(sketch, "E263.MirrorP", {"position": v(-68.18, -79.38) * mm});
            skPoint(sketch, "E264.MirrorP", {"position": v(-79.38, -87.28) * mm});
            skPoint(sketch, "E265.MirrorP", {"position": v(-85.78, -79.38) * mm});
            skPoint(sketch, "E266", {"position": v(0, 58.84) * mm});
            skPoint(sketch, "E267", {"position": v(0, 48.84) * mm});
            skCircle(sketch, "E268", {"center": v(0, 48.84) * mm, "radius": 1.6 * mm});
            skPoint(sketch, "E269", {"position": v(4.5, 49.84) * mm});
            skLineSegment(sketch, "E270", {"start": v(4.5, 49.84) * mm, "end": v(4.5, 47.84) * mm});
            skLineSegment(sketch, "E271.MirrorCS", {"start": v(-4.5, 49.84) * mm, "end": v(-4.5, 47.84) * mm});
            skPoint(sketch, "E272", {"position": v(10, 49.84) * mm});
            skLineSegment(sketch, "E273", {"start": v(10, 49.84) * mm, "end": v(10, 47.84) * mm});
            skLineSegment(sketch, "E274.MirrorCS", {"start": v(-10, 49.84) * mm, "end": v(-10, 47.84) * mm});
            skLineSegment(sketch, "E275.trimOffspring", {"start": v(-10, 49.84) * mm, "end": v(-4.5, 49.84) * mm});
            skLineSegment(sketch, "E276", {"start": v(-10, 47.84) * mm, "end": v(-4.5, 47.84) * mm});
            skLineSegment(sketch, "E277", {"start": v(4.5, 49.84) * mm, "end": v(10, 49.84) * mm});
            skLineSegment(sketch, "E278", {"start": v(4.5, 47.84) * mm, "end": v(10, 47.84) * mm});
            skArc(sketch, "E279", {"start": v(-25.3, -14.68) * mm, "mid": v(-19.2, 0) * mm, "end": v(-25.3, 14.68) * mm});
            skArc(sketch, "E280.MirrorCS", {"start": v(25.3, -14.68) * mm, "mid": v(19.2, 0) * mm, "end": v(25.3, 14.68) * mm});
            skPoint(sketch, "E281", {"position": v(0, -50.08) * mm});
            skLineSegment(sketch, "E282", {"start": v(0, -13.72) * mm, "end": v(-8.33, -0.45) * mm});
            skLineSegment(sketch, "E283", {"start": v(-8.33, -0.45) * mm, "end": v(0, 14.48) * mm});
            skLineSegment(sketch, "E284.MirrorCS", {"start": v(8.33, -0.45) * mm, "end": v(0, 14.48) * mm});
            skLineSegment(sketch, "E285.MirrorCS", {"start": v(0, -13.72) * mm, "end": v(8.33, -0.45) * mm});
            skLineSegment(sketch, "E286", {"start": v(-4.82, -26.55) * mm, "end": v(0, -18.88) * mm});
            skLineSegment(sketch, "E287.MirrorCS", {"start": v(4.82, -26.55) * mm, "end": v(0, -18.88) * mm});
            skLineSegment(sketch, "E288.MirrorCS", {"start": v(-4.82, -26.55) * mm, "end": v(0, -34.22) * mm});
            skLineSegment(sketch, "E289.MirrorCS", {"start": v(4.82, -26.55) * mm, "end": v(0, -34.22) * mm});
            skLineSegment(sketch, "E290.MirrorCS", {"start": v(4.82, 26.55) * mm, "end": v(0, 18.88) * mm});
            skLineSegment(sketch, "E291.MirrorCS", {"start": v(-4.82, 26.55) * mm, "end": v(0, 18.88) * mm});
            skLineSegment(sketch, "E292.MirrorCS", {"start": v(4.82, 26.55) * mm, "end": v(0, 34.22) * mm});
            skLineSegment(sketch, "E293.MirrorCS", {"start": v(-4.82, 26.55) * mm, "end": v(0, 34.22) * mm});
            skSolve(sketch);
        }
        {
            var Q0;
            {var subQ5=sQuery(id+"F0.wireOp",EDGE,"E25");Q0=makeQuery(id+"F0.imprint","IMPRINT",FACE,{"disambiguationData":[TD([[makeQuery(id+"F0.imprint","IMPRINT",EDGE,{"derivedFrom":subQ5}),-1.0]])]});}
            var Q1;
            Q1=makeQuery(id+"F0.imprint","IMPRINT",FACE,{"disambiguationData":[TD([[makeQuery(id+"F0.imprint","IMPRINT",EDGE,{"derivedFrom":sQuery(id+"F0.wireOp",EDGE,"ee434ed6-9a63-42d5-9ff3-101a510c28ad")}),-1.0]])]});
            var Q2;
            {var subQ0=sQuery(id+"F0.wireOp",EDGE,"f8f53325-3871-4694-9a1a-c58136c1004540.MirrorCS");var subQ5=sQuery(id+"F0.wireOp",EDGE,"7bc29fb5-4c99-461b-938b-c9a8d298ebd630.MirrorCS");var subQ6=makeQuery(id+"F0.imprint","INTERSECT",VERTEX,{"derivedFrom":[subQ5,subQ0]});Q2=makeQuery(id+"F0.imprint","IMPRINT",FACE,{"disambiguationData":[TD([[makeQuery(id+"F0.imprint","IMPRINT",EDGE,{"disambiguationData":[TD([[subQ6,-1.0]])],"derivedFrom":subQ5}),-1.0]])]});}
            var Q3;
            {var subQ0=sQuery(id+"F0.wireOp",EDGE,"f8f53325-3871-4694-9a1a-c58136c1004557.MirrorCS");var subQ1=sQuery(id+"F0.wireOp",EDGE,"a115e07c-bb1e-43a8-8170-9e804958d2362.MirrorCS");var subQ2=makeQuery(id+"F0.imprint","INTERSECT",VERTEX,{"derivedFrom":[subQ1,subQ0]});Q3=makeQuery(id+"F0.imprint","IMPRINT",FACE,{"disambiguationData":[TD([[makeQuery(id+"F0.imprint","IMPRINT",EDGE,{"disambiguationData":[TD([[subQ2,-1.0]])],"derivedFrom":subQ1}),1.0]])]});}
            var Q4;
            {var subQ3=sQuery(id+"F0.wireOp",EDGE,"f8f53325-3871-4694-9a1a-c58136c1004543.MirrorCS");Q4=makeQuery(id+"F0.imprint","IMPRINT",FACE,{"disambiguationData":[TD([[makeQuery(id+"F0.imprint","IMPRINT",EDGE,{"derivedFrom":subQ3}),1.0]])]});}
            var Q5;
            {var subQ3=sQuery(id+"F0.wireOp",EDGE,"f8f53325-3871-4694-9a1a-c58136c1004543.MirrorCS");Q5=makeQuery(id+"F0.imprint","IMPRINT",FACE,{"disambiguationData":[TD([[makeQuery(id+"F0.imprint","IMPRINT",EDGE,{"derivedFrom":subQ3}),-1.0]])]});}
            var Q6;
            {var subQ7=sQuery(id+"F0.wireOp",EDGE,"f8f53325-3871-4694-9a1a-c58136c1004553.MirrorCS");var subQ9=makeQuery(id+"F0.imprint","IMPRINT",VERTEX,{"derivedFrom":subQ7});Q6=makeQuery(id+"F0.imprint","IMPRINT",FACE,{"disambiguationData":[TD([[makeQuery(id+"F0.imprint","IMPRINT",EDGE,{"disambiguationData":[TD([[subQ9,1.0]])],"derivedFrom":subQ7}),-1.0]])]});}
            var Q7;
            {var subQ1=sQuery(id+"F0.wireOp",EDGE,"7bc29fb5-4c99-461b-938b-c9a8d298ebd630.MirrorCS");var subQ3=sQuery(id+"F0.wireOp",EDGE,"f8f53325-3871-4694-9a1a-c58136c1004540.MirrorCS");var subQ4=makeQuery(id+"F0.imprint","INTERSECT",VERTEX,{"derivedFrom":[subQ1,subQ3]});Q7=makeQuery(id+"F0.imprint","IMPRINT",FACE,{"disambiguationData":[TD([[makeQuery(id+"F0.imprint","IMPRINT",EDGE,{"disambiguationData":[TD([[subQ4,-1.0]])],"derivedFrom":subQ3}),-1.0]])]});}
            var Q8;
            {var subQ0=sQuery(id+"F0.wireOp",EDGE,"dc22e482-73c7-4c7b-b6e4-16479c9313ed.trimOffspring");var subQ1=makeQuery(id+"F0.imprint","IMPRINT",VERTEX,{"derivedFrom":subQ0});Q8=makeQuery(id+"F0.imprint","IMPRINT",FACE,{"disambiguationData":[TD([[makeQuery(id+"F0.imprint","IMPRINT",EDGE,{"disambiguationData":[TD([[subQ1,-1.0]])],"derivedFrom":subQ0}),-1.0]])]});}
            var Q9;
            {var subQ0=sQuery(id+"F0.wireOp",EDGE,"dc22e482-73c7-4c7b-b6e4-16479c9313ed.trimOffspring");var subQ1=makeQuery(id+"F0.imprint","IMPRINT",VERTEX,{"derivedFrom":subQ0});Q9=makeQuery(id+"F0.imprint","IMPRINT",FACE,{"disambiguationData":[TD([[makeQuery(id+"F0.imprint","IMPRINT",EDGE,{"disambiguationData":[TD([[subQ1,-1.0]])],"derivedFrom":subQ0}),1.0]])]});}
            var Q10;
            {var subQ5=sQuery(id+"F0.wireOp",EDGE,"o4Odivwz-GYB5-zOQl-xJ8i-PzwIrLdqennX");Q10=makeQuery(id+"F0.imprint","IMPRINT",FACE,{"disambiguationData":[TD([[makeQuery(id+"F0.imprint","IMPRINT",EDGE,{"derivedFrom":subQ5}),-1.0]])]});}
            var Q11;
            {var subQ1=sQuery(id+"F0.wireOp",EDGE,"E11.trimOffspring");var subQ5=sQuery(id+"F0.wireOp",EDGE,"084885b6-39b8-4495-b3d9-620cf64acb16.0");var subQ6=makeQuery(id+"F0.imprint","INTERSECT",VERTEX,{"derivedFrom":[subQ5,subQ1]});Q11=makeQuery(id+"F0.imprint","IMPRINT",FACE,{"disambiguationData":[TD([[makeQuery(id+"F0.imprint","IMPRINT",EDGE,{"disambiguationData":[TD([[subQ6,-1.0]])],"derivedFrom":subQ1}),1.0]])]});}
            var Q12;
            {var subQ5=sQuery(id+"F0.wireOp",EDGE,"o4Odivwz-GYB5-zOQl-xJ8i-PzwIrLdqennX");Q12=makeQuery(id+"F0.imprint","IMPRINT",FACE,{"disambiguationData":[TD([[makeQuery(id+"F0.imprint","IMPRINT",EDGE,{"derivedFrom":subQ5}),1.0]])]});}
            var Q13;
            Q13=makeQuery(id+"F0.imprint","IMPRINT",FACE,{"disambiguationData":[TD([[makeQuery(id+"F0.imprint","IMPRINT",EDGE,{"derivedFrom":sQuery(id+"F0.wireOp",EDGE,"E13.MirrorC")}),1.0]])]});
            var Q14;
            {var subQ8=sQuery(id+"F0.wireOp",EDGE,"7bc29fb5-4c99-461b-938b-c9a8d298ebd615.MirrorCS");Q14=makeQuery(id+"F0.imprint","IMPRINT",FACE,{"disambiguationData":[TD([[makeQuery(id+"F0.imprint","IMPRINT",EDGE,{"derivedFrom":subQ8}),1.0]])]});}
            var Q15;
            {var subQ5=sQuery(id+"F0.wireOp",EDGE,"E134.MirrorCS");var subQ7=sQuery(id+"F0.wireOp",EDGE,"E135.MirrorCS");var subQ8=makeQuery(id+"F0.imprint","INTERSECT",VERTEX,{"derivedFrom":[subQ5,subQ7]});Q15=makeQuery(id+"F0.imprint","IMPRINT",FACE,{"disambiguationData":[TD([[makeQuery(id+"F0.imprint","IMPRINT",EDGE,{"disambiguationData":[TD([[subQ8,-1.0]])],"derivedFrom":subQ7}),-1.0]])]});}
            var Q16;
            {var subQ6=sQuery(id+"F0.wireOp",EDGE,"b3c935ba-b9cf-4cd1-9b47-664a38c8914e.trimOffspring");Q16=makeQuery(id+"F0.imprint","IMPRINT",FACE,{"disambiguationData":[TD([[makeQuery(id+"F0.imprint","IMPRINT",EDGE,{"derivedFrom":subQ6}),-1.0]])]});}
            var Q17;
            {var subQ7=sQuery(id+"F0.wireOp",EDGE,"b3c935ba-b9cf-4cd1-9b47-664a38c8914e.trimOffspring");Q17=makeQuery(id+"F0.imprint","IMPRINT",FACE,{"disambiguationData":[TD([[makeQuery(id+"F0.imprint","IMPRINT",EDGE,{"derivedFrom":subQ7}),1.0]])]});}
            var Q18;
            {var subQ0=sQuery(id+"F0.wireOp",EDGE,"E35");Q18=makeQuery(id+"F0.imprint","IMPRINT",FACE,{"disambiguationData":[TD([[makeQuery(id+"F0.imprint","IMPRINT",EDGE,{"derivedFrom":subQ0}),-1.0]])]});}
            var Q19;
            {var subQ3=sQuery(id+"F0.wireOp",EDGE,"E36.MirrorCS");Q19=makeQuery(id+"F0.imprint","IMPRINT",FACE,{"disambiguationData":[TD([[makeQuery(id+"F0.imprint","IMPRINT",EDGE,{"derivedFrom":subQ3}),1.0]])]});}
            var Q20;
            {var subQ5=sQuery(id+"F0.wireOp",EDGE,"f8f53325-3871-4694-9a1a-c58136c1004557.MirrorCS");var subQ6=makeQuery(id+"F0.imprint","IMPRINT",VERTEX,{"derivedFrom":subQ5});Q20=makeQuery(id+"F0.imprint","IMPRINT",FACE,{"disambiguationData":[TD([[makeQuery(id+"F0.imprint","IMPRINT",EDGE,{"disambiguationData":[TD([[subQ6,1.0]])],"derivedFrom":subQ5}),1.0]])]});}
            var Q21;
            {var subQ3=sQuery(id+"F0.wireOp",EDGE,"f8f53325-3871-4694-9a1a-c58136c1004539.MirrorCS");var subQ7=sQuery(id+"F0.wireOp",EDGE,"f8f53325-3871-4694-9a1a-c58136c1004557.MirrorCS");var subQ9=makeQuery(id+"F0.imprint","INTERSECT",VERTEX,{"derivedFrom":[subQ3,subQ7]});Q21=makeQuery(id+"F0.imprint","IMPRINT",FACE,{"disambiguationData":[TD([[makeQuery(id+"F0.imprint","IMPRINT",EDGE,{"disambiguationData":[TD([[subQ9,-1.0]])],"derivedFrom":subQ3}),1.0]])]});}
            var Q22;
            {var subQ0=sQuery(id+"F0.wireOp",EDGE,"f8f53325-3871-4694-9a1a-c58136c1004532.MirrorCS");Q22=makeQuery(id+"F0.imprint","IMPRINT",FACE,{"disambiguationData":[TD([[makeQuery(id+"F0.imprint","IMPRINT",EDGE,{"derivedFrom":subQ0}),-1.0]])]});}
            var Q23;
            {var subQ4=sQuery(id+"F0.wireOp",EDGE,"f8f53325-3871-4694-9a1a-c58136c1004544.MirrorCS");Q23=makeQuery(id+"F0.imprint","IMPRINT",FACE,{"disambiguationData":[TD([[makeQuery(id+"F0.imprint","IMPRINT",EDGE,{"derivedFrom":subQ4}),1.0]])]});}
            var Q24;
            {var subQ6=sQuery(id+"F0.wireOp",EDGE,"f8f53325-3871-4694-9a1a-c58136c1004537.MirrorCS");Q24=makeQuery(id+"F0.imprint","IMPRINT",FACE,{"disambiguationData":[TD([[makeQuery(id+"F0.imprint","IMPRINT",EDGE,{"derivedFrom":subQ6}),-1.0]])]});}
            var Q25;
            {var subQ2=sQuery(id+"F0.wireOp",EDGE,"f8f53325-3871-4694-9a1a-c58136c1004546.MirrorCS");var subQ4=sQuery(id+"F0.wireOp",EDGE,"f8f53325-3871-4694-9a1a-c58136c1004553.MirrorCS");var subQ5=makeQuery(id+"F0.imprint","INTERSECT",VERTEX,{"derivedFrom":[subQ2,subQ4]});Q25=makeQuery(id+"F0.imprint","IMPRINT",FACE,{"disambiguationData":[TD([[makeQuery(id+"F0.imprint","IMPRINT",EDGE,{"disambiguationData":[TD([[subQ5,-1.0]])],"derivedFrom":subQ2}),-1.0]])]});}
            var Q26;
            Q26=makeQuery(id+"F0.imprint","IMPRINT",FACE,{"disambiguationData":[TD([[makeQuery(id+"F0.imprint","IMPRINT",EDGE,{"derivedFrom":sQuery(id+"F0.wireOp",EDGE,"E16.MirrorC")}),-1.0]])]});
            var Q27;
            {var subQ0=sQuery(id+"F0.wireOp",EDGE,"f8f53325-3871-4694-9a1a-c58136c1004538.MirrorCS");Q27=makeQuery(id+"F0.imprint","IMPRINT",FACE,{"disambiguationData":[TD([[makeQuery(id+"F0.imprint","IMPRINT",EDGE,{"derivedFrom":subQ0}),1.0]])]});}
            var Q28;
            {var subQ3=sQuery(id+"F0.wireOp",EDGE,"9ea1215f-6162-4539-8bb0-dced369ac285");Q28=makeQuery(id+"F0.imprint","IMPRINT",FACE,{"disambiguationData":[TD([[makeQuery(id+"F0.imprint","IMPRINT",EDGE,{"derivedFrom":subQ3}),1.0]])]});}
            var Q29;
            {var subQ3=sQuery(id+"F0.wireOp",EDGE,"Zu9wmFt8-NIoA-l1hR-vEso-LH5LRDH4uiVa");Q29=makeQuery(id+"F0.imprint","IMPRINT",FACE,{"disambiguationData":[TD([[makeQuery(id+"F0.imprint","IMPRINT",EDGE,{"derivedFrom":subQ3}),-1.0]])]});}
            var Q30;
            {var subQ1=sQuery(id+"F0.wireOp",EDGE,"a115e07c-bb1e-43a8-8170-9e804958d2362.MirrorCS");var subQ3=sQuery(id+"F0.wireOp",EDGE,"1812a963-9c49-4839-8543-119de58bcdd85.MirrorCS");var subQ4=makeQuery(id+"F0.imprint","INTERSECT",VERTEX,{"derivedFrom":[subQ1,subQ3]});Q30=makeQuery(id+"F0.imprint","IMPRINT",FACE,{"disambiguationData":[TD([[makeQuery(id+"F0.imprint","IMPRINT",EDGE,{"disambiguationData":[TD([[subQ4,1.0]])],"derivedFrom":subQ1}),-1.0]])]});}
            var Q31;
            {var subQ3=sQuery(id+"F0.wireOp",EDGE,"JGGKBNC8-gyzP-dW2Y-ju0s-WTFlYiPE1KVv");Q31=makeQuery(id+"F0.imprint","IMPRINT",FACE,{"disambiguationData":[TD([[makeQuery(id+"F0.imprint","IMPRINT",EDGE,{"derivedFrom":subQ3}),-1.0]])]});}
            var Q32;
            {var subQ0=sQuery(id+"F0.wireOp",EDGE,"E33.MirrorCS");Q32=makeQuery(id+"F0.imprint","IMPRINT",FACE,{"disambiguationData":[TD([[makeQuery(id+"F0.imprint","IMPRINT",EDGE,{"derivedFrom":subQ0}),-1.0]])]});}
            var Q33;
            {var subQ0=sQuery(id+"F0.wireOp",EDGE,"JGGKBNC8-gyzP-dW2Y-ju0s-WTFlYiPE1KVv");Q33=makeQuery(id+"F0.imprint","IMPRINT",FACE,{"disambiguationData":[TD([[makeQuery(id+"F0.imprint","IMPRINT",EDGE,{"derivedFrom":subQ0}),1.0]])]});}
            var Q34;
            {var subQ0=sQuery(id+"F0.wireOp",EDGE,"Zu9wmFt8-NIoA-l1hR-vEso-LH5LRDH4uiVa");Q34=makeQuery(id+"F0.imprint","IMPRINT",FACE,{"disambiguationData":[TD([[makeQuery(id+"F0.imprint","IMPRINT",EDGE,{"derivedFrom":subQ0}),1.0]])]});}
            var Q35;
            {var subQ0=sQuery(id+"F0.wireOp",EDGE,"YEz6IhFE-E22z-fM7U-7GAN-Xr5mP4M5U6VH");Q35=makeQuery(id+"F0.imprint","IMPRINT",FACE,{"disambiguationData":[TD([[makeQuery(id+"F0.imprint","IMPRINT",EDGE,{"derivedFrom":subQ0}),-1.0]])]});}
            var Q36;
            Q36=makeQuery(id+"F0.imprint","IMPRINT",FACE,{"disambiguationData":[TD([[makeQuery(id+"F0.imprint","IMPRINT",EDGE,{"derivedFrom":sQuery(id+"F0.wireOp",EDGE,"E15.MirrorC")}),1.0]])]});
            var Q37;
            {var subQ0=sQuery(id+"F0.wireOp",EDGE,"E4.MirrorCS");Q37=makeQuery(id+"F0.imprint","IMPRINT",FACE,{"disambiguationData":[TD([[makeQuery(id+"F0.imprint","IMPRINT",EDGE,{"derivedFrom":subQ0}),1.0]])]});}
            var Q38;
            {var subQ0=sQuery(id+"F0.wireOp",EDGE,"E132.MirrorCS");Q38=makeQuery(id+"F0.imprint","IMPRINT",FACE,{"disambiguationData":[TD([[makeQuery(id+"F0.imprint","IMPRINT",EDGE,{"derivedFrom":subQ0}),-1.0]])]});}
            extrude(context, id + "F1", {"entities" : qUnion([Q0, Q1, Q2, Q3, Q4, Q5, Q6, Q7, Q8, Q9, Q10, Q11, Q12, Q13, Q14, Q15, Q16, Q17, Q18, Q19, Q20, Q21, Q22, Q23, Q24, Q25, Q26, Q27, Q28, Q29, Q30, Q31, Q32, Q33, Q34, Q35, Q36, Q37, Q38]), "depth" : 4 * mm, "offsetDistance" : 25 * mm});
        }
        {
            var Q0;
            Q0 = qSketchRegion(id + "F0", true);
            extrude(context, id + "F2", {"entities" : qUnion([Q0]), "operationType" : NewBodyOperationType.ADD, "depth" : 4 * mm, "offsetDistance" : 25 * mm});
        }
    });
